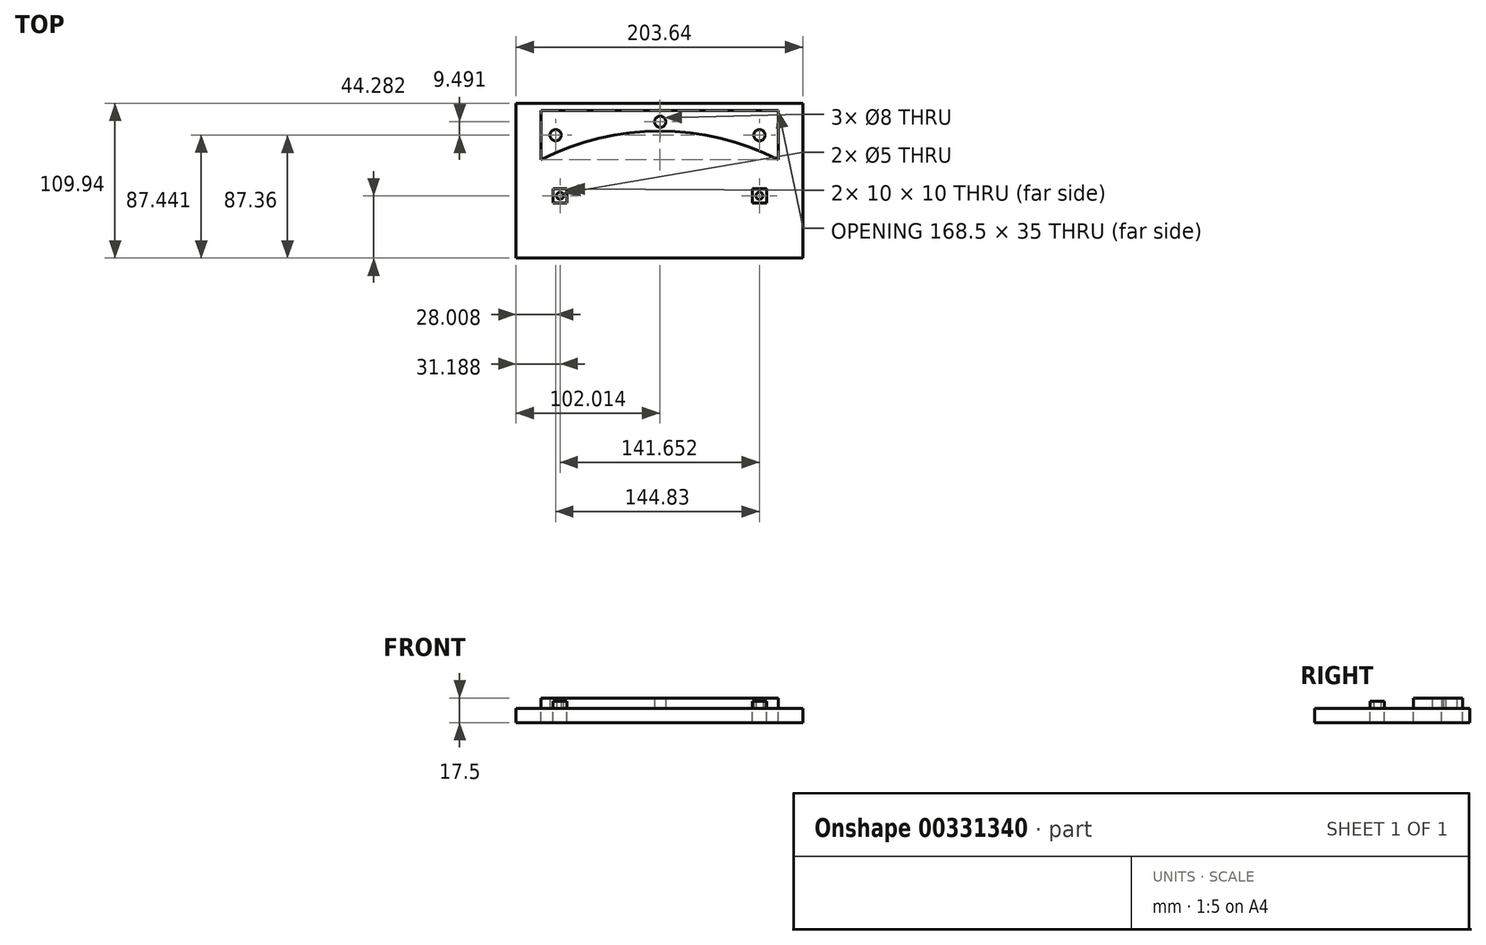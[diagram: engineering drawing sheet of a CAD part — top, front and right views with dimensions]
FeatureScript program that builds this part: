
annotation { "Feature Type Name" : "Feature", "Feature Type Description" : "" }
export const myFeature = defineFeature(function(context is Context, id is Id, definition is map)
    precondition{}
    {
        {
            var Q0;
            Q0=qCreatedBy(makeId("Top.planeOp"),FACE);
            var sketch = newSketch(context, id + "F0", { "sketchPlane" : qUnion([Q0])});
            skLineSegment(sketch, "E0.bottom", {"start": v(101.82, -54.97) * mm, "end": v(-101.82, -54.97) * mm});
            skLineSegment(sketch, "E0.top", {"start": v(101.82, 54.97) * mm, "end": v(-101.82, 54.97) * mm});
            skLineSegment(sketch, "E0.left", {"start": v(101.82, -54.97) * mm, "end": v(101.82, 54.97) * mm});
            skLineSegment(sketch, "E0.right", {"start": v(-101.82, -54.97) * mm, "end": v(-101.82, 54.97) * mm});
            skPoint(sketch, "E0.middle", {"position": v(0, 0) * mm});
            skLineSegment(sketch, "E1.0", {"start": v(84.46, 49.97) * mm, "end": v(-84.06, 49.97) * mm});
            skLineSegment(sketch, "E2", {"start": v(-84.06, 49.97) * mm, "end": v(-84.06, 14.97) * mm});
            skLineSegment(sketch, "E3.0", {"start": v(84.44, 49.97) * mm, "end": v(84.44, 14.97) * mm});
            skCircle(sketch, "E4", {"center": v(-73.81, 32.39) * mm, "radius": 4 * mm});
            skCircle(sketch, "E5", {"center": v(71.02, 32.39) * mm, "radius": 4 * mm});
            skArc(sketch, "E6", {"start": v(84.44, 14.97) * mm, "mid": v(0.2, 35.21) * mm, "end": v(-84.06, 14.97) * mm});
            skCircle(sketch, "E7", {"center": v(0.52, 41.88) * mm, "radius": 4 * mm});
            skArc(sketch, "E8.0", {"start": v(66.02, -8.26) * mm, "mid": v(0.2, 6.26) * mm, "end": v(-65.63, -8.26) * mm});
            skLineSegment(sketch, "E9.bottom", {"start": v(-65.63, -15.69) * mm, "end": v(-75.63, -15.69) * mm});
            skLineSegment(sketch, "E9.top", {"start": v(-65.63, -5.69) * mm, "end": v(-75.63, -5.69) * mm});
            skLineSegment(sketch, "E9.left", {"start": v(-65.63, -15.69) * mm, "end": v(-65.63, -5.69) * mm});
            skLineSegment(sketch, "E9.right", {"start": v(-75.63, -15.69) * mm, "end": v(-75.63, -5.69) * mm});
            skPoint(sketch, "E9.middle", {"position": v(-70.63, -10.69) * mm});
            skLineSegment(sketch, "E10.bottom", {"start": v(76.02, -15.69) * mm, "end": v(66.02, -15.69) * mm});
            skLineSegment(sketch, "E10.top", {"start": v(76.02, -5.69) * mm, "end": v(66.02, -5.69) * mm});
            skLineSegment(sketch, "E10.left", {"start": v(76.02, -15.69) * mm, "end": v(76.02, -5.69) * mm});
            skLineSegment(sketch, "E10.right", {"start": v(66.02, -15.69) * mm, "end": v(66.02, -5.69) * mm});
            skPoint(sketch, "E10.middle", {"position": v(71.02, -10.69) * mm});
            skCircle(sketch, "E11", {"center": v(-70.63, -10.69) * mm, "radius": 2.5 * mm});
            skCircle(sketch, "E12", {"center": v(71.02, -10.69) * mm, "radius": 2.5 * mm});
            skSolve(sketch);
        }
        {
            var Q0;
            {var subQ1=sQuery(id+"F0.wireOp",EDGE,"E2");Q0=makeQuery(id+"F0.imprint","IMPRINT",FACE,{"disambiguationData":[TD([[makeQuery(id+"F0.imprint","IMPRINT",EDGE,{"derivedFrom":subQ1}),1.0]])]});}
            extrude(context, id + "F1", {"entities" : qUnion([Q0]), "depth" : 7.5 * mm});
        }
        {
            var Q0;
            {var subQ3=sQuery(id+"F0.wireOp",EDGE,"E9.bottom");Q0=makeQuery(id+"F0.imprint","IMPRINT",FACE,{"disambiguationData":[TD([[makeQuery(id+"F0.imprint","IMPRINT",EDGE,{"derivedFrom":subQ3}),-1.0]])]});}
            var Q1;
            {var subQ2=sQuery(id+"F0.wireOp",EDGE,"E10.bottom");Q1=makeQuery(id+"F0.imprint","IMPRINT",FACE,{"disambiguationData":[TD([[makeQuery(id+"F0.imprint","IMPRINT",EDGE,{"derivedFrom":subQ2}),-1.0]])]});}
            extrude(context, id + "F2", {"entities" : qUnion([Q0, Q1]), "depth" : 5 * mm});
        }
        {
            var Q0;
            Q0=sQuery(id+"F0.wireOp",EDGE,"E8.0");
            extrude(context, id + "F3", {"bodyType" : ToolBodyType.SURFACE, "surfaceEntities" : qUnion([Q0]), "depth" : 5 * mm, "hasSecondDirection" : true, "secondDirectionOppositeDirection" : true, "secondDirectionDepth" : -2 * mm});
        }
        {
            var Q0;
            Q0=makeQuery(id+"F0.imprint","IMPRINT",FACE,{"disambiguationData":[TD([[makeQuery(id+"F0.imprint","IMPRINT",EDGE,{"derivedFrom":sQuery(id+"F0.wireOp",EDGE,"E0.bottom")}),-1.0]])]});
            extrude(context, id + "F4", {"entities" : qUnion([Q0]), "oppositeDirection" : true, "depth" : 10 * mm});
        }
    });
